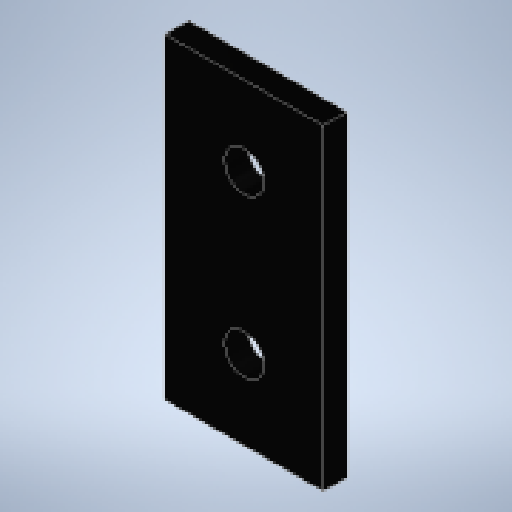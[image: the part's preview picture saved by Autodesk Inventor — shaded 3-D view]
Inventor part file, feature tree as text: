
AUTODESK INVENTOR PART (.ipt)
format: ipt  version: 2025.1 (Build 291241020, 241B)  size: 233,984 bytes
history: native  units: mm
features: extrude x1, sketch x1
ambient origin geometry x8: Origin, YZ Plane, XZ Plane, XY Plane, X Axis, Y Axis, Z Axis, Center Point
bodies: Solid1 (feature_tree)
feature tree (2):
  extrude  "Extrusion1"  Depth=20.0mm
  sketch  "Sketch1"  dims[d0=40.0mm d1=20.0mm d2=5.0mm d3=20.0mm d4=10.0mm d5=10.0mm d6=3.0mm d7=0.0mm]
